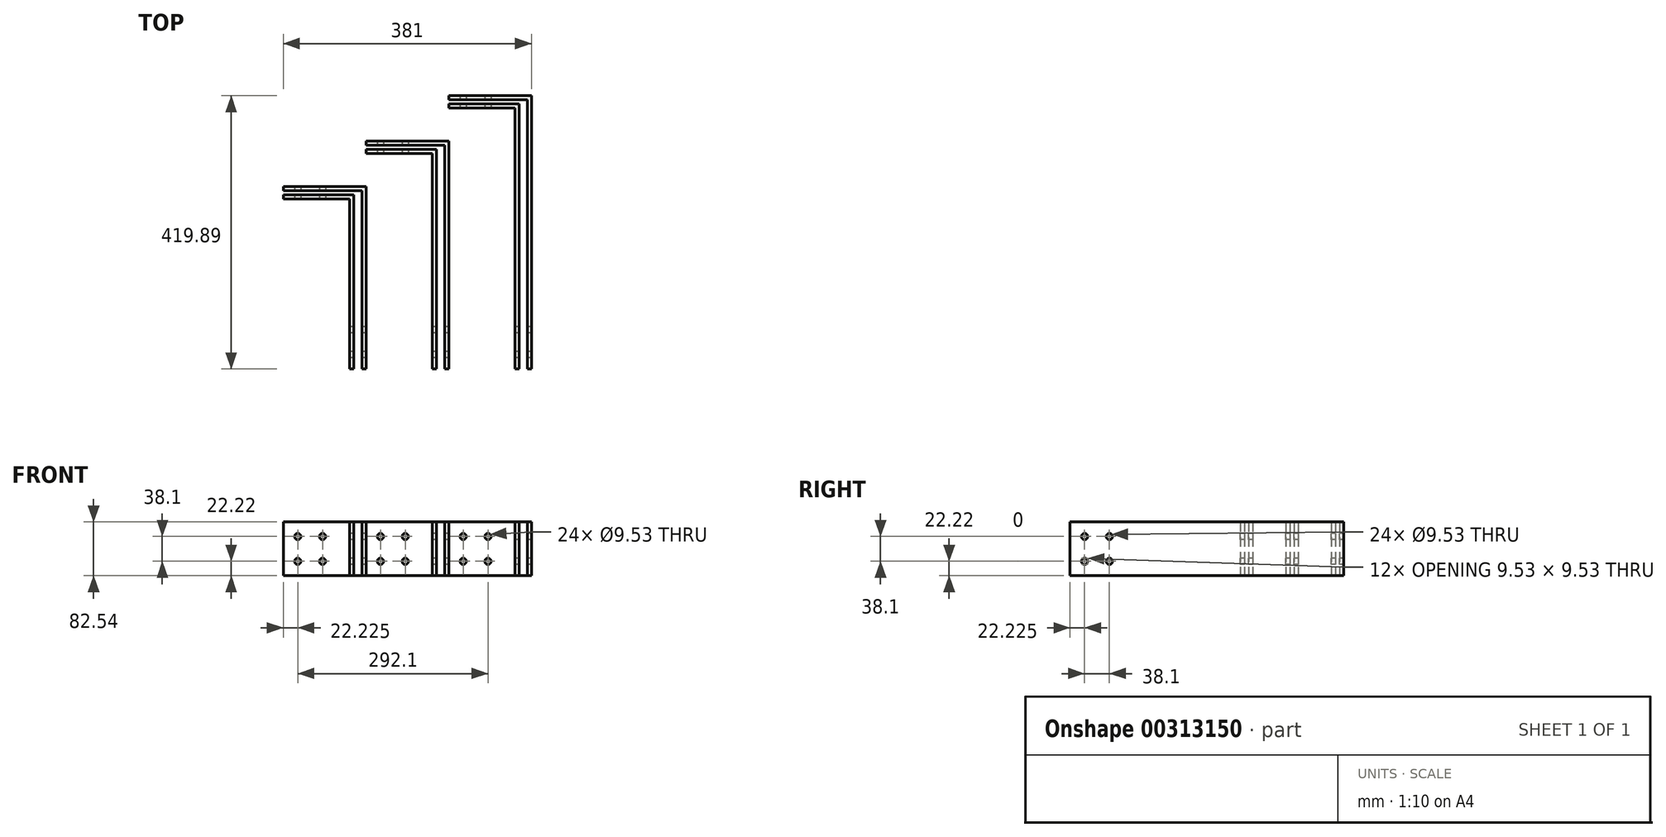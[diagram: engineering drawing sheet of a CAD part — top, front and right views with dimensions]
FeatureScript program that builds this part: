
annotation { "Feature Type Name" : "Feature", "Feature Type Description" : "" }
export const myFeature = defineFeature(function(context is Context, id is Id, definition is map)
    precondition{}
    {
        {
            var Q0;
            Q0=qCreatedBy(makeId("Top.planeOp"),FACE);
            var sketch = newSketch(context, id + "F0", { "sketchPlane" : qUnion([Q0])});
            skLineSegment(sketch, "E0.bottom", {"start": v(0, 0) * mm, "end": v(6.35, 0) * mm});
            skLineSegment(sketch, "E0.left", {"start": v(0, 0) * mm, "end": v(0, 261.14) * mm});
            skLineSegment(sketch, "E1.bottom", {"start": v(19.05, 0) * mm, "end": v(25.4, 0) * mm});
            skLineSegment(sketch, "E1.left", {"start": v(19.05, 0) * mm, "end": v(19.05, 273.84) * mm});
            skLineSegment(sketch, "E2", {"start": v(0, 261.14) * mm, "end": v(-101.6, 261.14) * mm});
            skLineSegment(sketch, "E3", {"start": v(-101.6, 261.14) * mm, "end": v(-101.6, 267.49) * mm});
            skLineSegment(sketch, "E4", {"start": v(-101.6, 267.49) * mm, "end": v(6.35, 267.49) * mm});
            skLineSegment(sketch, "E5", {"start": v(6.35, 267.49) * mm, "end": v(6.35, 0) * mm});
            skLineSegment(sketch, "E6", {"start": v(19.05, 273.84) * mm, "end": v(-101.6, 273.84) * mm});
            skLineSegment(sketch, "E7", {"start": v(-101.6, 273.84) * mm, "end": v(-101.6, 280.19) * mm});
            skLineSegment(sketch, "E8", {"start": v(-101.6, 280.19) * mm, "end": v(25.4, 280.19) * mm});
            skLineSegment(sketch, "E9", {"start": v(25.4, 280.19) * mm, "end": v(25.4, 0) * mm});
            skLineSegment(sketch, "E10.bottom", {"start": v(127, 0) * mm, "end": v(133.35, 0) * mm});
            skLineSegment(sketch, "E10.left", {"start": v(127, 0) * mm, "end": v(127, 330.99) * mm});
            skLineSegment(sketch, "E11.bottom", {"start": v(146.05, 0) * mm, "end": v(152.4, 0) * mm});
            skLineSegment(sketch, "E11.left", {"start": v(146.05, 0) * mm, "end": v(146.05, 343.69) * mm});
            skLineSegment(sketch, "E12", {"start": v(127, 330.99) * mm, "end": v(25.4, 330.99) * mm});
            skLineSegment(sketch, "E13", {"start": v(25.4, 330.99) * mm, "end": v(25.4, 337.34) * mm});
            skLineSegment(sketch, "E14", {"start": v(25.4, 337.34) * mm, "end": v(133.35, 337.34) * mm});
            skLineSegment(sketch, "E15", {"start": v(133.35, 337.34) * mm, "end": v(133.35, 0) * mm});
            skLineSegment(sketch, "E16", {"start": v(146.05, 343.69) * mm, "end": v(25.4, 343.69) * mm});
            skLineSegment(sketch, "E17", {"start": v(25.4, 343.69) * mm, "end": v(25.4, 350.04) * mm});
            skLineSegment(sketch, "E18", {"start": v(25.4, 350.04) * mm, "end": v(152.4, 350.04) * mm});
            skLineSegment(sketch, "E19", {"start": v(152.4, 350.04) * mm, "end": v(152.4, 0) * mm});
            skLineSegment(sketch, "E20.bottom", {"start": v(254, 0) * mm, "end": v(260.35, 0) * mm});
            skLineSegment(sketch, "E20.left", {"start": v(254, 0) * mm, "end": v(254, 400.84) * mm});
            skLineSegment(sketch, "E21.bottom", {"start": v(273.05, 0) * mm, "end": v(279.4, 0) * mm});
            skLineSegment(sketch, "E21.left", {"start": v(273.05, 0) * mm, "end": v(273.05, 413.54) * mm});
            skLineSegment(sketch, "E22", {"start": v(254, 400.84) * mm, "end": v(152.4, 400.84) * mm});
            skLineSegment(sketch, "E23", {"start": v(152.4, 400.84) * mm, "end": v(152.4, 407.19) * mm});
            skLineSegment(sketch, "E24", {"start": v(152.4, 407.19) * mm, "end": v(260.35, 407.19) * mm});
            skLineSegment(sketch, "E25", {"start": v(260.35, 407.19) * mm, "end": v(260.35, 0) * mm});
            skLineSegment(sketch, "E26", {"start": v(273.05, 413.54) * mm, "end": v(152.4, 413.54) * mm});
            skLineSegment(sketch, "E27", {"start": v(152.4, 413.54) * mm, "end": v(152.4, 419.89) * mm});
            skLineSegment(sketch, "E28", {"start": v(152.4, 419.89) * mm, "end": v(279.4, 419.89) * mm});
            skLineSegment(sketch, "E29", {"start": v(279.4, 419.89) * mm, "end": v(279.4, 0) * mm});
            skSolve(sketch);
        }
        {
            var Q0;
            Q0=qSketchRegion(id+"F0",true);
            extrude(context, id + "F1", {"entities" : qUnion([Q0]), "endBound" : BoundingType.SYMMETRIC, "depth" : 82.55 * mm});
        }
        {
            var Q0;
            Q0=makeQuery(id+"F1.opExtrude","SWEPT_FACE",FACE,{"disambiguationData":[OSD([sQuery(id+"F0.wireOp",EDGE,"E0.left")])]});
            var sketch = newSketch(context, id + "F2", { "sketchPlane" : qUnion([Q0])});
            skCircle(sketch, "E30", {"center": v(-22.23, 19.05) * mm, "radius": 4.76 * mm});
            skCircle(sketch, "E31", {"center": v(-22.23, -19.05) * mm, "radius": 4.76 * mm});
            skCircle(sketch, "E32", {"center": v(-60.32, -19.05) * mm, "radius": 4.76 * mm});
            skCircle(sketch, "E33", {"center": v(-60.33, 19.05) * mm, "radius": 4.76 * mm});
            skSolve(sketch);
        }
        {
            var Q0;
            Q0=qSketchRegion(id+"F2",true);
            extrude(context, id + "F3", {"entities" : qUnion([Q0]), "operationType" : NewBodyOperationType.REMOVE, "endBound" : BoundingType.THROUGH_ALL, "oppositeDirection" : true, "depth" : 25.4 * mm, "hasSecondDirection" : true, "secondDirectionBound" : SecondDirectionBoundingType.THROUGH_ALL, "secondDirectionOppositeDirection" : false, "secondDirectionDepth" : 25.4 * mm});
        }
        {
            var Q0;
            Q0=makeQuery(id+"F1.opExtrude","SWEPT_FACE",FACE,{"disambiguationData":[OSD([sQuery(id+"F0.wireOp",EDGE,"E2")])]});
            var sketch = newSketch(context, id + "F4", { "sketchPlane" : qUnion([Q0])});
            skCircle(sketch, "E34", {"center": v(-79.37, 19.05) * mm, "radius": 4.76 * mm});
            skCircle(sketch, "E35", {"center": v(-79.37, -19.05) * mm, "radius": 4.76 * mm});
            skCircle(sketch, "E36", {"center": v(-41.27, -19.05) * mm, "radius": 4.76 * mm});
            skCircle(sketch, "E37", {"center": v(-41.27, 19.05) * mm, "radius": 4.76 * mm});
            skCircle(sketch, "E38.1.0.0", {"center": v(47.63, 19.05) * mm, "radius": 4.76 * mm});
            skCircle(sketch, "E38.1.0.1", {"center": v(47.63, -19.05) * mm, "radius": 4.76 * mm});
            skCircle(sketch, "E38.1.0.2", {"center": v(85.73, -19.05) * mm, "radius": 4.76 * mm});
            skCircle(sketch, "E38.1.0.3", {"center": v(85.73, 19.05) * mm, "radius": 4.76 * mm});
            skCircle(sketch, "E38.2.0.0", {"center": v(174.63, 19.05) * mm, "radius": 4.76 * mm});
            skCircle(sketch, "E38.2.0.1", {"center": v(174.63, -19.05) * mm, "radius": 4.76 * mm});
            skCircle(sketch, "E38.2.0.2", {"center": v(212.73, -19.05) * mm, "radius": 4.76 * mm});
            skCircle(sketch, "E38.2.0.3", {"center": v(212.73, 19.05) * mm, "radius": 4.76 * mm});
            skLineSegment(sketch, "E38.direction1", {"start": v(-79.37, -19.05) * mm, "end": v(47.63, -19.05) * mm, "construction": true});
            skSolve(sketch);
        }
        {
            var Q0;
            Q0 = qSketchRegion(id + "F4", true);
            extrude(context, id + "F5", {"entities" : qUnion([Q0]), "operationType" : NewBodyOperationType.REMOVE, "endBound" : BoundingType.THROUGH_ALL, "oppositeDirection" : true, "depth" : 25.4 * mm});
        }
    });
